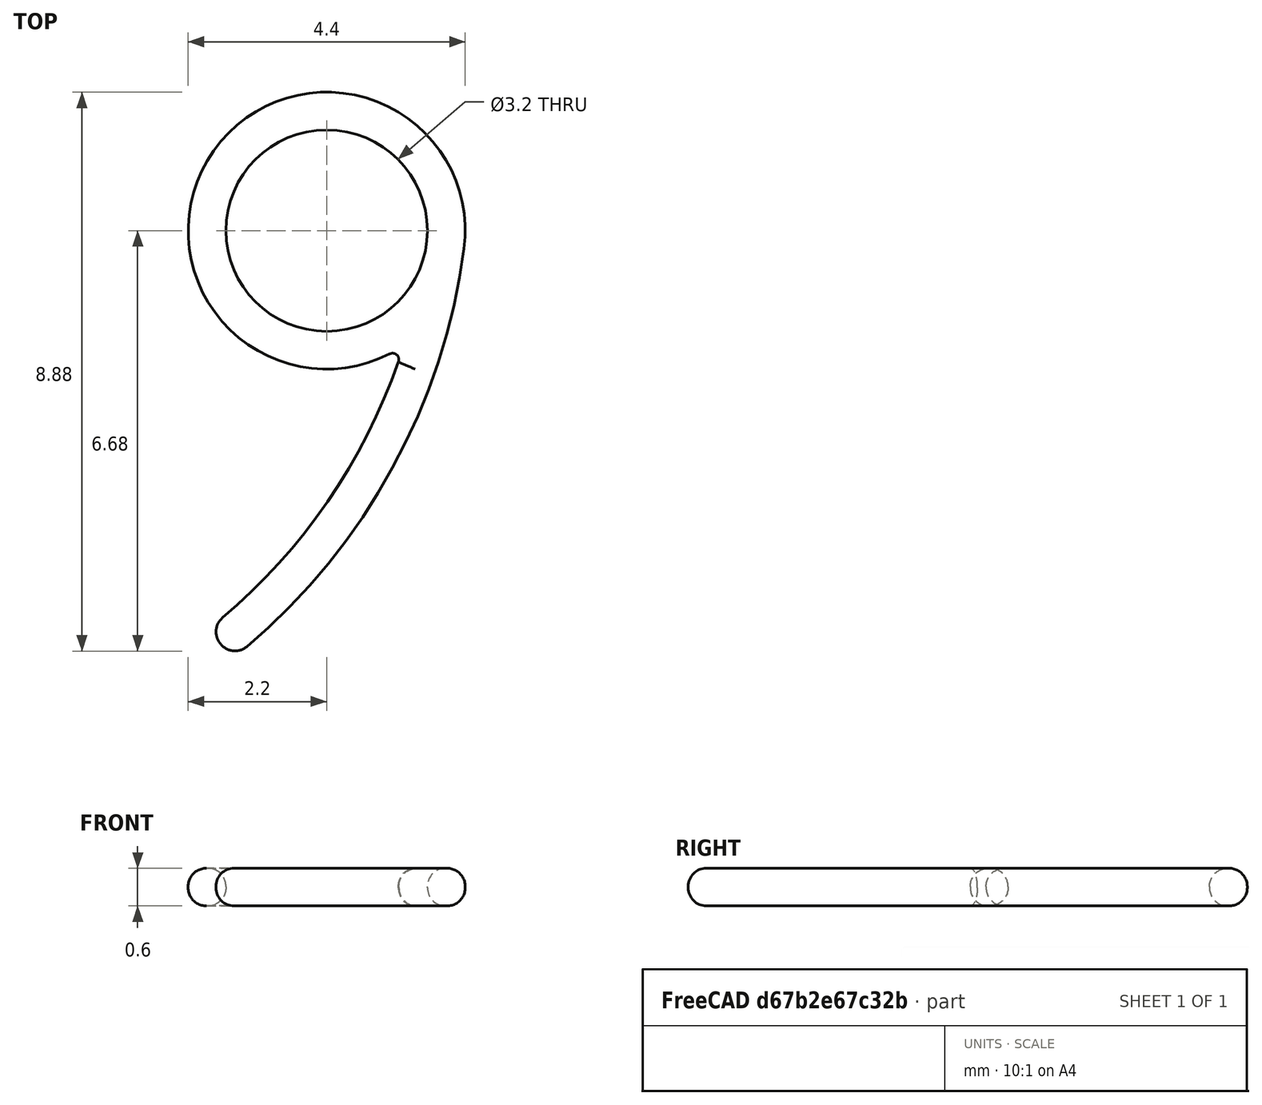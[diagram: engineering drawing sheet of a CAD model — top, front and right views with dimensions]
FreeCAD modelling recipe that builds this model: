
FCSTD DOCUMENT  (FreeCAD 0.16R6712 (Git))
Label: 9s
License: All rights reserved
LicenseURL: http://en.wikipedia.org/wiki/All_rights_reserved
objects: Sketcher::SketchObject×1, PartDesign::Pad×1, PartDesign::Fillet×1, Mesh::Feature×1
note: 4 computed .brp shape members not serialized (recipe doc carries the construction recipe); baked Part::Feature solids carry a one-line shape summary decoded from their .brp

FEATURE [Sketcher::SketchObject] Sketch
  sketch-geometry (6):
    g0: ArcOfCircle CenterX=-7.73305 CenterY=7.81979 CenterZ=0 NormalX=0 NormalY=0 NormalZ=1 Radius=10 StartAngle=5.38535 EndAngle=6.15207
    g1: ArcOfCircle CenterX=-7.73305 CenterY=7.81979 CenterZ=0 NormalX=0 NormalY=0 NormalZ=1 Radius=9.4 StartAngle=5.38535 EndAngle=5.94631
    g2: LineSegment StartX=-1.87398 StartY=0.469187 StartZ=0 EndX=-1.5 EndY=0 EndZ=0
    g3: ArcOfCircle CenterX=1.0466 CenterY=4.75192 CenterZ=0 NormalX=0 NormalY=0 NormalZ=1 Radius=0.1 StartAngle=5.88043 EndAngle=8.32644
    g4: ArcOfCircle CenterX=0 CenterY=6.8 CenterZ=0 NormalX=0 NormalY=0 NormalZ=1 Radius=2.2 StartAngle=6.15206 EndAngle=11.468
    g5: Circle CenterX=0 CenterY=6.8 CenterZ=0 NormalX=0 NormalY=0 NormalZ=1 Radius=1.6
  constraints (20):
    c: PointOnObject(g0,g-1)
    c: Radius(g0) = 10
    c: Coincident(g1,g0)
    c: Radius(g1) = 9.4
    c: Coincident(g2,g0)
    c: PointOnObject(g1,g2)
    c: Perpendicular(g1,g2,g1) = 4.71239
    c: Coincident(g1,g2)
    c: DistanceX(g-2,g0) = -1.5
    c: PointOnObject(g3,g1)
    c: Coincident(g3,g1)
    c: PointOnObject(g4,g-2)
    c: Coincident(g4,g3)
    c: Coincident(g4,g0)
    c: Radius(g4) = 2.2
    c: Coincident(g5,g4)
    c: Radius(g5) = 1.6
    c: DistanceY(g-1,g4) = 6.8
    c: Radius(g3) = 0.1
    c: Tangent(g3,g4)
FEATURE [PartDesign::Pad] Pad
  Length = 0.6
  Length2 = 100
  Midplane = true
  Sketch = -> Sketch
  Type = 0
FEATURE [PartDesign::Fillet] Fillet
  Base = -> Pad [Edge4,Edge7,Edge10,Edge13,Edge15,Edge18,Edge1,Edge2,Edge3,Edge6,Edge9,Edge12,Edge14,Edge17]
  Radius = 0.29
FEATURE [Mesh::Feature] Mesh  label="Fillet (Meshed)"
